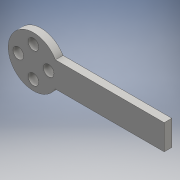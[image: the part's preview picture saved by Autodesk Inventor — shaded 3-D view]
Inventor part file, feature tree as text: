
AUTODESK INVENTOR PART (.ipt)
format: ipt  version: 2016 (Build 200138000, 138)  size: 112,640 bytes
history: native  units: mm
features: extrude x1, sketch x1
ambient origin geometry x8: Origin, YZ Plane, XZ Plane, XY Plane, X Axis, Y Axis, Z Axis, Center Point
bodies: Solid1 (feature_tree)
feature tree (2):
  extrude  "Extrusion1"  Depth=3.0mm
  sketch  "Sketch1"  dims[d0=20.0mm d1=4.25mm d2=6.0mm d3=4.25mm d4=6.0mm d5=4.25mm d6=6.0mm d7=4.25mm d8=6.0mm d9=4.0mm d22=3.0mm d23=0.0mm d26=43.0mm d28=43.0mm]
